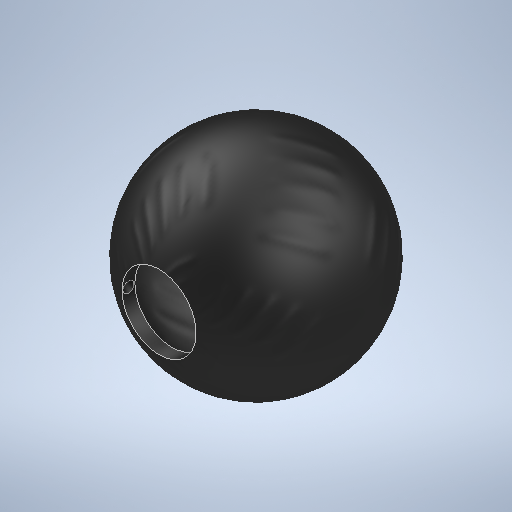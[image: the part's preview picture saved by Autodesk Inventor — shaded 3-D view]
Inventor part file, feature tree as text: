
AUTODESK INVENTOR PART (.ipt)
format: ipt  version: 2025.2 (Build 292293000, 293)  size: 344,064 bytes
history: native  units: mm
features: sketch x3, revolve x2, extrude x1
ambient origin geometry x8: Origin, YZ Plane, XZ Plane, XY Plane, X Axis, Y Axis, Z Axis, Center Point
bodies: Solid1 (feature_tree)
feature tree (6):
  revolve  "Revolution1"  [1 undecoded]
  revolve  "Revolution2"  [1 undecoded]
  extrude  "Extrusion1"  TaperAngle=360.0deg  [1 undecoded]
  sketch  "Sketch1"  dims[d4=0.8mm d5=7.0mm]
  sketch  "Sketch3"  dims[d6=0.7mm d7=6.6mm]
  sketch  "Sketch4"  dims[d9=360.0deg d10=360.0deg d13=5.0mm d14=50.0mm d15=0.0mm]
note: 3 required parameter values undecoded (feature->parameter linkage not recoverable at this tier; creation-order binding heuristic only, values carry confidence <= 0.55)